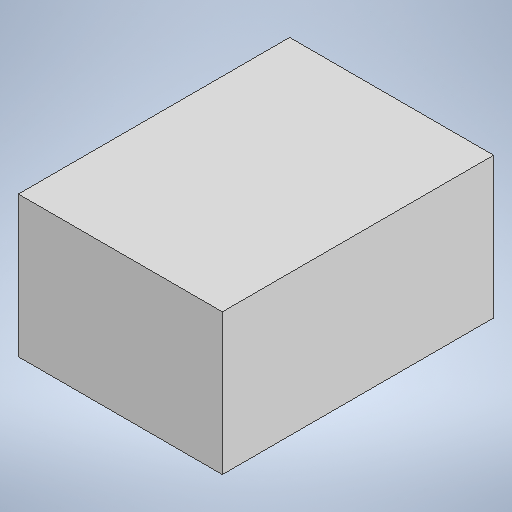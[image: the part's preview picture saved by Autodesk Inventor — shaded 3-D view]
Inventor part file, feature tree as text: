
AUTODESK INVENTOR PART (.ipt)
format: ipt  version: 2025.2 (Build 292293000, 293)  size: 164,864 bytes
history: native  units: mm
features: extrude x1, sketch x1
ambient origin geometry x8: Origin, YZ Plane, XZ Plane, XY Plane, X Axis, Y Axis, Z Axis, Center Point
bodies: Solid1 (feature_tree)
feature tree (2):
  extrude  "Extrusion1"  Depth=215.952mm
  sketch  "Sketch1"  dims[d0=162.4mm d1=215.952mm d2=112.2mm d3=0.0mm]
